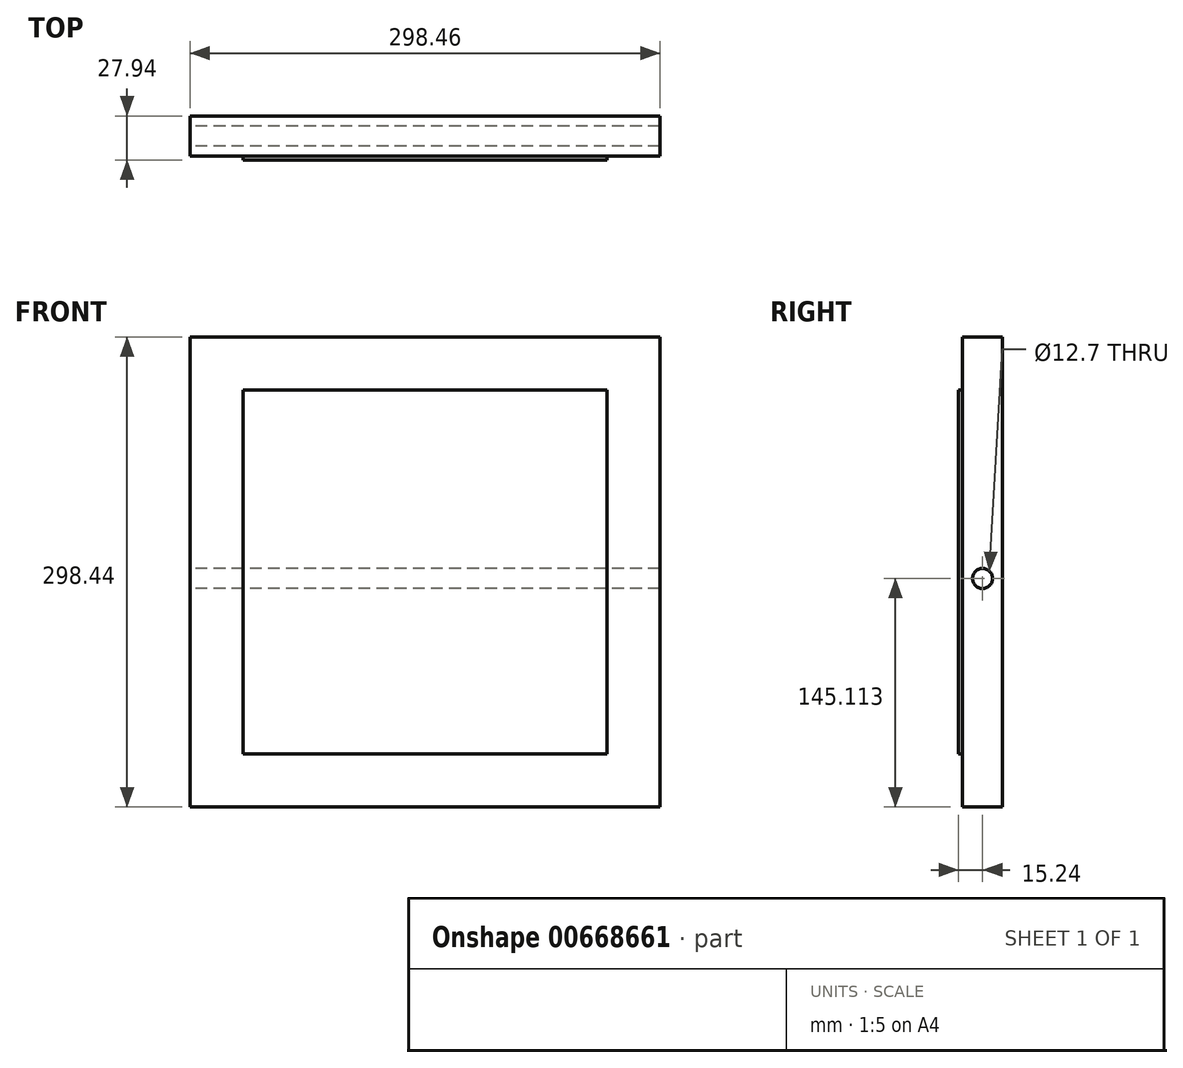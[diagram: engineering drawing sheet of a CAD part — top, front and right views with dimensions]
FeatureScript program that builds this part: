
annotation { "Feature Type Name" : "Feature", "Feature Type Description" : "" }
export const myFeature = defineFeature(function(context is Context, id is Id, definition is map)
    precondition{}
    {
        {
            var Q0;
            Q0=qCreatedBy(makeId("Right.planeOp"),FACE);
            var sketch = newSketch(context, id + "F0", { "sketchPlane" : qUnion([Q0])});
            skLineSegment(sketch, "E0.bottom", {"start": v(12.7, 149.23) * mm, "end": v(-12.7, 149.23) * mm});
            skLineSegment(sketch, "E0.top", {"start": v(12.7, -149.23) * mm, "end": v(-12.7, -149.23) * mm});
            skLineSegment(sketch, "E0.left", {"start": v(12.7, 149.23) * mm, "end": v(12.7, -149.23) * mm});
            skLineSegment(sketch, "E0.right", {"start": v(-12.7, 149.23) * mm, "end": v(-12.7, -149.23) * mm});
            skPoint(sketch, "E0.middle", {"position": v(0, 0) * mm});
            skCircle(sketch, "E1", {"center": v(0, -4.1) * mm, "radius": 6.35 * mm});
            skSolve(sketch);
        }
        {
            var Q0;
            Q0=makeQuery(id+"F0.imprint","IMPRINT",FACE,{"disambiguationData":[TD([[makeQuery(id+"F0.imprint","IMPRINT",EDGE,{"derivedFrom":sQuery(id+"F0.wireOp",EDGE,"E0.bottom")}),1.0]])]});
            extrude(context, id + "F1", {"entities" : qUnion([Q0]), "endBound" : BoundingType.SYMMETRIC, "depth" : 298.45 * mm, "offsetDistance" : 25.4 * mm});
        }
        {
            var Q0;
            Q0=makeQuery(id+"F1.opExtrude","SWEPT_FACE",FACE,{"disambiguationData":[OSD([sQuery(id+"F0.wireOp",EDGE,"E0.right")])]});
            var sketch = newSketch(context, id + "F2", { "sketchPlane" : qUnion([Q0])});
            skLineSegment(sketch, "E2", {"start": v(-115.63, 115.63) * mm, "end": v(-115.63, -115.63) * mm});
            skLineSegment(sketch, "E3", {"start": v(-115.63, -115.63) * mm, "end": v(115.63, -115.63) * mm});
            skLineSegment(sketch, "E4", {"start": v(115.63, -115.63) * mm, "end": v(115.63, 115.63) * mm});
            skLineSegment(sketch, "E5", {"start": v(115.63, 115.63) * mm, "end": v(-115.63, 115.63) * mm});
            skSolve(sketch);
        }
        {
            var Q0;
            Q0=makeQuery(id+"F2.imprint","IMPRINT",FACE,{"disambiguationData":[TD([[makeQuery(id+"F2.imprint","IMPRINT",EDGE,{"derivedFrom":sQuery(id+"F2.wireOp",EDGE,"E2")}),1.0]])]});
            extrude(context, id + "F3", {"entities" : qUnion([Q0]), "operationType" : NewBodyOperationType.ADD, "endBound" : BoundingType.SYMMETRIC, "depth" : 5.08 * mm, "offsetDistance" : 25.4 * mm});
        }
    });
